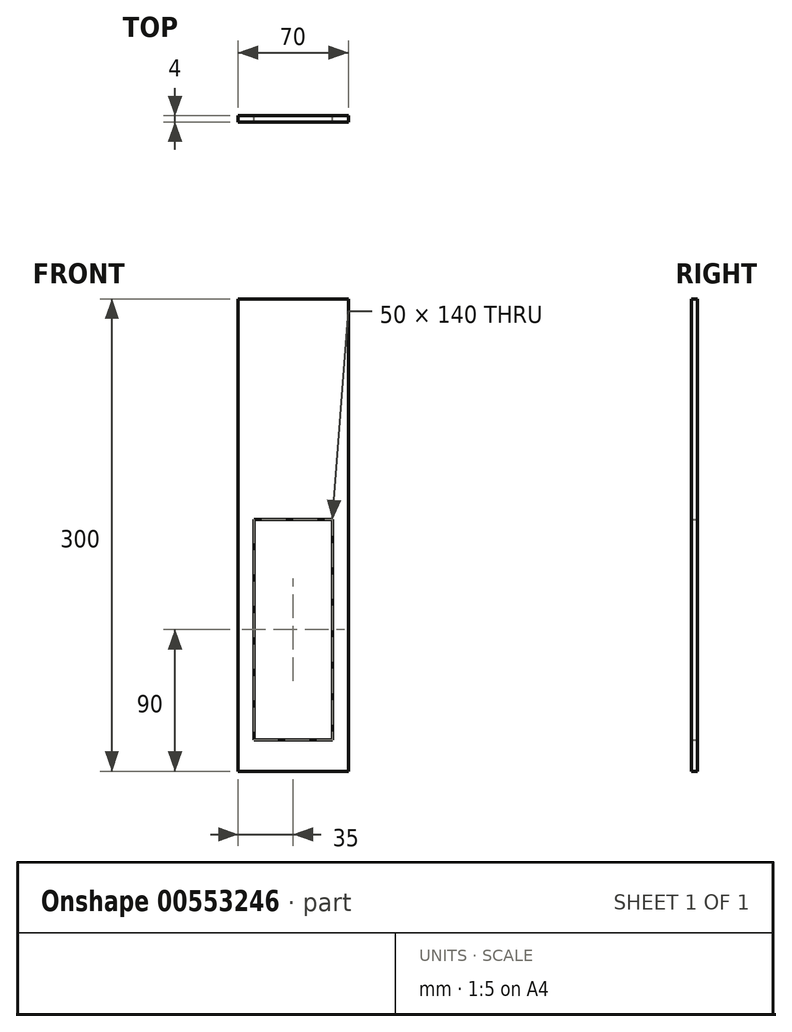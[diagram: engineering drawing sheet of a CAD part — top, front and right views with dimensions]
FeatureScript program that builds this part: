
annotation { "Feature Type Name" : "Feature", "Feature Type Description" : "" }
export const myFeature = defineFeature(function(context is Context, id is Id, definition is map)
    precondition{}
    {
        {
            var Q0;
            Q0=qCreatedBy(makeId("Front.planeOp"),FACE);
            var sketch = newSketch(context, id + "F0", { "sketchPlane" : qUnion([Q0])});
            skLineSegment(sketch, "E0", {"start": v(0, 0) * mm, "end": v(-70, 0) * mm});
            skLineSegment(sketch, "E1", {"start": v(-70, 0) * mm, "end": v(-70, 300) * mm});
            skLineSegment(sketch, "E2", {"start": v(-70, 300) * mm, "end": v(0, 300) * mm});
            skLineSegment(sketch, "E3", {"start": v(0, 300) * mm, "end": v(0, 0) * mm});
            skLineSegment(sketch, "E4", {"start": v(0, 300) * mm, "end": v(0, 192.07) * mm});
            skLineSegment(sketch, "E5", {"start": v(0, 300) * mm, "end": v(-10, 300) * mm});
            skLineSegment(sketch, "E6", {"start": v(-70, 300) * mm, "end": v(-60, 300) * mm});
            skLineSegment(sketch, "E7", {"start": v(-60, 300) * mm, "end": v(-60, 0) * mm});
            skLineSegment(sketch, "E8", {"start": v(-10, 300) * mm, "end": v(-10, 0) * mm});
            skLineSegment(sketch, "E9", {"start": v(-10, 300) * mm, "end": v(-10, 160) * mm});
            skLineSegment(sketch, "E10", {"start": v(-10, 160) * mm, "end": v(-10, 140) * mm});
            skLineSegment(sketch, "E11", {"start": v(-10, 140) * mm, "end": v(-10, 120) * mm});
            skLineSegment(sketch, "E12", {"start": v(-10, 120) * mm, "end": v(-10, 100) * mm});
            skLineSegment(sketch, "E13", {"start": v(-10, 100) * mm, "end": v(-10, 80) * mm});
            skLineSegment(sketch, "E14", {"start": v(-10, 80) * mm, "end": v(-10, 60) * mm});
            skLineSegment(sketch, "E15", {"start": v(-10, 60) * mm, "end": v(-10, 40) * mm});
            skLineSegment(sketch, "E16", {"start": v(-10, 40) * mm, "end": v(-10, 20) * mm});
            skLineSegment(sketch, "E17", {"start": v(-60, 300) * mm, "end": v(-60, 160) * mm});
            skLineSegment(sketch, "E18", {"start": v(-60, 160) * mm, "end": v(-60, 140) * mm});
            skLineSegment(sketch, "E19", {"start": v(-60, 140) * mm, "end": v(-60, 120) * mm});
            skLineSegment(sketch, "E20", {"start": v(-60, 120) * mm, "end": v(-60, 100) * mm});
            skLineSegment(sketch, "E21", {"start": v(-60, 100) * mm, "end": v(-60, 80) * mm});
            skLineSegment(sketch, "E22", {"start": v(-60, 80) * mm, "end": v(-60, 60) * mm});
            skLineSegment(sketch, "E23", {"start": v(-60, 60) * mm, "end": v(-60, 40) * mm});
            skLineSegment(sketch, "E24", {"start": v(-60, 40) * mm, "end": v(-60, 20) * mm});
            skLineSegment(sketch, "E25", {"start": v(-60, 20) * mm, "end": v(-10, 20) * mm});
            skLineSegment(sketch, "E26", {"start": v(-10, 40) * mm, "end": v(-60, 40) * mm});
            skLineSegment(sketch, "E27", {"start": v(-60, 60) * mm, "end": v(-10, 60) * mm});
            skLineSegment(sketch, "E28", {"start": v(-10, 80) * mm, "end": v(-60, 80) * mm});
            skLineSegment(sketch, "E29", {"start": v(-60, 100) * mm, "end": v(-10, 100) * mm});
            skLineSegment(sketch, "E30", {"start": v(-10, 120) * mm, "end": v(-60, 120) * mm});
            skLineSegment(sketch, "E31", {"start": v(-60, 140) * mm, "end": v(-10, 140) * mm});
            skLineSegment(sketch, "E32", {"start": v(-10, 160) * mm, "end": v(-60, 160) * mm});
            skLineSegment(sketch, "E33", {"start": v(-10, 20) * mm, "end": v(-10, 23) * mm});
            skLineSegment(sketch, "E34", {"start": v(-10, 23) * mm, "end": v(-60, 23) * mm});
            skLineSegment(sketch, "E35", {"start": v(-60, 23) * mm, "end": v(-60, 20) * mm});
            skSolve(sketch);
        }
        {
            var Q0;
            Q0 = qSketchRegion(id + "F0", true);
            var Q1;
            Q1=makeQuery(id+"F0.imprint","IMPRINT",FACE,{"disambiguationData":[TD([[makeQuery(id+"F0.imprint","IMPRINT",EDGE,{"derivedFrom":sQuery(id+"F0.wireOp",EDGE,"E10")}),-1.0]])]});
            var Q2;
            Q2=makeQuery(id+"F0.imprint","IMPRINT",FACE,{"disambiguationData":[TD([[makeQuery(id+"F0.imprint","IMPRINT",EDGE,{"derivedFrom":sQuery(id+"F0.wireOp",EDGE,"E12")}),-1.0]])]});
            var Q3;
            Q3=makeQuery(id+"F0.imprint","IMPRINT",FACE,{"disambiguationData":[TD([[makeQuery(id+"F0.imprint","IMPRINT",EDGE,{"derivedFrom":sQuery(id+"F0.wireOp",EDGE,"E13")}),-1.0]])]});
            var Q4;
            Q4=makeQuery(id+"F0.imprint","IMPRINT",FACE,{"disambiguationData":[TD([[makeQuery(id+"F0.imprint","IMPRINT",EDGE,{"derivedFrom":sQuery(id+"F0.wireOp",EDGE,"E11")}),-1.0]])]});
            var Q5;
            Q5=makeQuery(id+"F0.imprint","IMPRINT",FACE,{"disambiguationData":[TD([[makeQuery(id+"F0.imprint","IMPRINT",EDGE,{"derivedFrom":sQuery(id+"F0.wireOp",EDGE,"E15")}),-1.0]])]});
            var Q6;
            Q6=makeQuery(id+"F0.imprint","IMPRINT",FACE,{"disambiguationData":[TD([[makeQuery(id+"F0.imprint","IMPRINT",EDGE,{"derivedFrom":sQuery(id+"F0.wireOp",EDGE,"E14")}),-1.0]])]});
            var Q7;
            Q7=makeQuery(id+"F0.imprint","IMPRINT",FACE,{"disambiguationData":[TD([[makeQuery(id+"F0.imprint","IMPRINT",EDGE,{"derivedFrom":sQuery(id+"F0.wireOp",EDGE,"E16")}),-1.0]])]});
            extrude(context, id + "F1", {"entities" : qUnion([Q0, Q1, Q2, Q3, Q4, Q5, Q6, Q7]), "depth" : 4 * mm, "offsetDistance" : 25 * mm});
        }
    });
